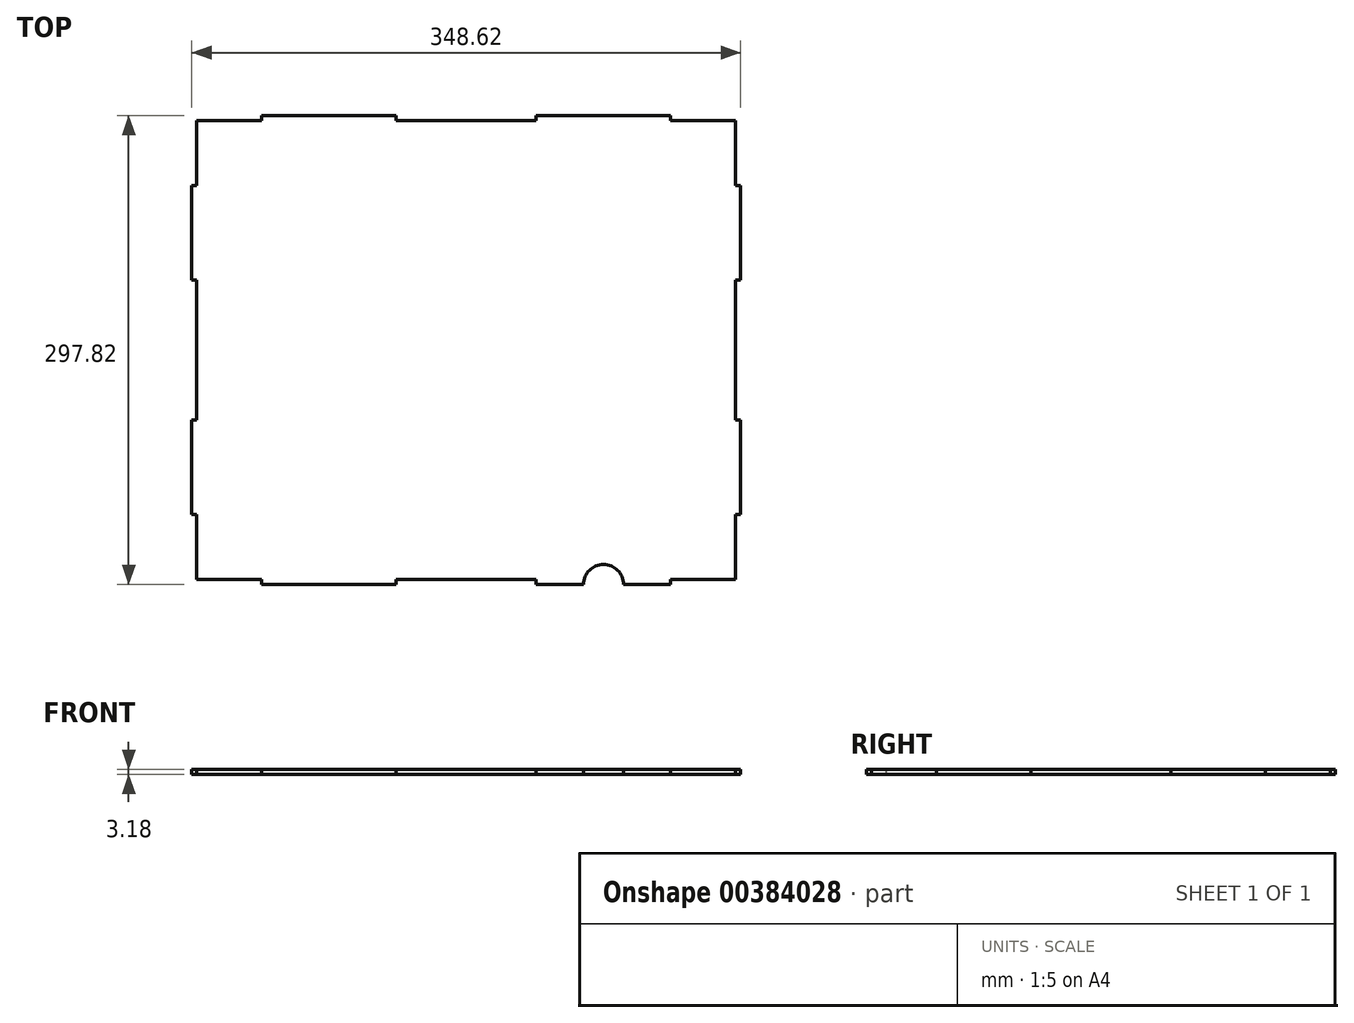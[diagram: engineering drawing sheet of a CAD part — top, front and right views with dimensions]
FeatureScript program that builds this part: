
annotation { "Feature Type Name" : "Feature", "Feature Type Description" : "" }
export const myFeature = defineFeature(function(context is Context, id is Id, definition is map)
    precondition{}
    {
        {
            var Q0;
            Q0=qCreatedBy(makeId("Top.planeOp"),FACE);
            var sketch = newSketch(context, id + "F0", { "sketchPlane" : qUnion([Q0])});
            skLineSegment(sketch, "E0.bottom", {"start": v(-174.3, 148.9) * mm, "end": v(174.3, 148.9) * mm});
            skLineSegment(sketch, "E0.top", {"start": v(-174.3, -148.9) * mm, "end": v(174.3, -148.9) * mm});
            skLineSegment(sketch, "E0.left", {"start": v(-174.3, 148.9) * mm, "end": v(-174.3, -148.9) * mm});
            skLineSegment(sketch, "E0.right", {"start": v(174.3, 148.9) * mm, "end": v(174.3, -148.9) * mm});
            skSolve(sketch);
        }
        {
            var Q0;
            Q0 = qSketchRegion(id + "F0", true);
            extrude(context, id + "F1", {"entities" : qUnion([Q0]), "depth" : 3.17 * mm});
        }
        {
            var Q0;
            Q0=makeQuery(id+"F1.opExtrude","CAP_FACE",FACE,{"disambiguationData":[OSD([sQuery(id+"F0.wireOp",EDGE,"E0.bottom"),sQuery(id+"F0.wireOp",EDGE,"E0.top"),sQuery(id+"F0.wireOp",EDGE,"E0.left"),sQuery(id+"F0.wireOp",EDGE,"E0.right")])],"isStart":false});
            var sketch = newSketch(context, id + "F2", { "sketchPlane" : qUnion([Q0])});
            skLineSegment(sketch, "E1", {"start": v(-129.86, 148.9) * mm, "end": v(-129.86, 145.73) * mm});
            skLineSegment(sketch, "E2", {"start": v(-129.86, 145.73) * mm, "end": v(-171.13, 145.73) * mm});
            skLineSegment(sketch, "E3", {"start": v(-171.13, 145.73) * mm, "end": v(-171.13, 104.46) * mm});
            skLineSegment(sketch, "E4", {"start": v(-171.13, 104.46) * mm, "end": v(-174.3, 104.46) * mm});
            skLineSegment(sketch, "E5", {"start": v(-174.3, 104.46) * mm, "end": v(-174.3, 148.9) * mm});
            skLineSegment(sketch, "E6", {"start": v(-174.3, 148.9) * mm, "end": v(-129.86, 148.9) * mm});
            skLineSegment(sketch, "E7.bottom", {"start": v(-44.45, 148.9) * mm, "end": v(0, 148.9) * mm});
            skLineSegment(sketch, "E7.top", {"start": v(-44.45, 145.73) * mm, "end": v(0, 145.73) * mm});
            skLineSegment(sketch, "E7.left", {"start": v(-44.45, 148.9) * mm, "end": v(-44.45, 145.73) * mm});
            skLineSegment(sketch, "E7.right", {"start": v(0, 148.9) * mm, "end": v(0, 145.73) * mm});
            skLineSegment(sketch, "E8.bottom", {"start": v(-174.3, 0) * mm, "end": v(-171.13, 0) * mm});
            skLineSegment(sketch, "E8.top", {"start": v(-174.3, 44.45) * mm, "end": v(-171.13, 44.45) * mm});
            skLineSegment(sketch, "E8.left", {"start": v(-174.3, 0) * mm, "end": v(-174.3, 44.45) * mm});
            skLineSegment(sketch, "E8.right", {"start": v(-171.13, 0) * mm, "end": v(-171.13, 44.45) * mm});
            skLineSegment(sketch, "E9.MirrorCS", {"start": v(44.45, 148.9) * mm, "end": v(44.45, 145.73) * mm});
            skLineSegment(sketch, "E10.MirrorCS", {"start": v(174.3, 0) * mm, "end": v(171.13, 0) * mm});
            skLineSegment(sketch, "E11.MirrorCS", {"start": v(174.3, 44.45) * mm, "end": v(171.13, 44.45) * mm});
            skLineSegment(sketch, "E12.MirrorCS", {"start": v(171.13, 104.46) * mm, "end": v(174.3, 104.46) * mm});
            skLineSegment(sketch, "E13.MirrorCS", {"start": v(129.86, 148.9) * mm, "end": v(129.86, 145.73) * mm});
            skLineSegment(sketch, "E14.MirrorCS", {"start": v(44.45, 145.73) * mm, "end": v(0, 145.73) * mm});
            skLineSegment(sketch, "E15.MirrorCS", {"start": v(174.3, 0) * mm, "end": v(174.3, 44.45) * mm});
            skLineSegment(sketch, "E16.MirrorCS", {"start": v(44.45, 148.9) * mm, "end": v(0, 148.9) * mm});
            skLineSegment(sketch, "E17.MirrorCS", {"start": v(171.13, 0) * mm, "end": v(171.13, 44.45) * mm});
            skLineSegment(sketch, "E18.MirrorCS", {"start": v(174.3, 148.9) * mm, "end": v(129.86, 148.9) * mm});
            skLineSegment(sketch, "E19.MirrorCS", {"start": v(174.3, 104.46) * mm, "end": v(174.3, 148.9) * mm});
            skLineSegment(sketch, "E20.MirrorCS", {"start": v(129.86, 145.73) * mm, "end": v(171.13, 145.73) * mm});
            skLineSegment(sketch, "E21.MirrorCS", {"start": v(171.13, 145.73) * mm, "end": v(171.13, 104.46) * mm});
            skLineSegment(sketch, "E22.MirrorCS", {"start": v(0, -148.9) * mm, "end": v(0, -145.73) * mm});
            skLineSegment(sketch, "E23.MirrorCS", {"start": v(-171.13, -104.46) * mm, "end": v(-174.3, -104.46) * mm});
            skLineSegment(sketch, "E24.MirrorCS", {"start": v(-129.86, -148.9) * mm, "end": v(-129.86, -145.73) * mm});
            skLineSegment(sketch, "E25.MirrorCS", {"start": v(44.45, -148.9) * mm, "end": v(44.45, -145.73) * mm});
            skLineSegment(sketch, "E26.MirrorCS", {"start": v(174.3, -44.45) * mm, "end": v(171.13, -44.45) * mm});
            skLineSegment(sketch, "E27.MirrorCS", {"start": v(129.86, -148.9) * mm, "end": v(129.86, -145.73) * mm});
            skLineSegment(sketch, "E28.MirrorCS", {"start": v(171.13, -104.46) * mm, "end": v(174.3, -104.46) * mm});
            skLineSegment(sketch, "E29.MirrorCS", {"start": v(-44.45, -148.9) * mm, "end": v(-44.45, -145.73) * mm});
            skLineSegment(sketch, "E30.MirrorCS", {"start": v(-174.3, -44.45) * mm, "end": v(-171.13, -44.45) * mm});
            skLineSegment(sketch, "E31.MirrorCS", {"start": v(-44.45, -148.9) * mm, "end": v(0, -148.9) * mm});
            skLineSegment(sketch, "E32.MirrorCS", {"start": v(-174.3, -148.9) * mm, "end": v(-129.86, -148.9) * mm});
            skLineSegment(sketch, "E33.MirrorCS", {"start": v(-174.3, -104.46) * mm, "end": v(-174.3, -148.9) * mm});
            skLineSegment(sketch, "E34.MirrorCS", {"start": v(-171.13, -145.73) * mm, "end": v(-171.13, -104.46) * mm});
            skLineSegment(sketch, "E35.MirrorCS", {"start": v(-129.86, -145.73) * mm, "end": v(-171.13, -145.73) * mm});
            skLineSegment(sketch, "E36.MirrorCS", {"start": v(-171.13, 0) * mm, "end": v(-171.13, -44.45) * mm});
            skLineSegment(sketch, "E37.MirrorCS", {"start": v(174.3, 0) * mm, "end": v(174.3, -44.45) * mm});
            skLineSegment(sketch, "E38.MirrorCS", {"start": v(174.3, -148.9) * mm, "end": v(129.86, -148.9) * mm});
            skLineSegment(sketch, "E39.MirrorCS", {"start": v(129.86, -145.73) * mm, "end": v(171.13, -145.73) * mm});
            skLineSegment(sketch, "E40.MirrorCS", {"start": v(44.45, -145.73) * mm, "end": v(0, -145.73) * mm});
            skLineSegment(sketch, "E41.MirrorCS", {"start": v(44.45, -148.9) * mm, "end": v(0, -148.9) * mm});
            skLineSegment(sketch, "E42.MirrorCS", {"start": v(171.13, 0) * mm, "end": v(171.13, -44.45) * mm});
            skLineSegment(sketch, "E43.MirrorCS", {"start": v(-44.45, -145.73) * mm, "end": v(0, -145.73) * mm});
            skLineSegment(sketch, "E44.MirrorCS", {"start": v(174.3, -104.46) * mm, "end": v(174.3, -148.9) * mm});
            skLineSegment(sketch, "E45.MirrorCS", {"start": v(171.13, -145.73) * mm, "end": v(171.13, -104.46) * mm});
            skLineSegment(sketch, "E46.MirrorCS", {"start": v(-174.3, 0) * mm, "end": v(-174.3, -44.45) * mm});
            skSolve(sketch);
        }
        {
            var Q0;
            Q0 = qSketchRegion(id + "F2", true);
            extrude(context, id + "F3", {"entities" : qUnion([Q0]), "operationType" : NewBodyOperationType.REMOVE, "endBound" : BoundingType.THROUGH_ALL, "oppositeDirection" : true, "depth" : 25.4 * mm});
        }
        {
            var Q0;
            Q0=makeQuery(id+"F1.opExtrude","CAP_FACE",FACE,{"disambiguationData":[OSD([sQuery(id+"F0.wireOp",EDGE,"E0.bottom"),sQuery(id+"F0.wireOp",EDGE,"E0.top"),sQuery(id+"F0.wireOp",EDGE,"E0.left"),sQuery(id+"F0.wireOp",EDGE,"E0.right")])],"isStart":false});
            var sketch = newSketch(context, id + "F4", { "sketchPlane" : qUnion([Q0])});
            skArc(sketch, "E47", {"start": v(99.85, -148.9) * mm, "mid": v(87.15, -136.2) * mm, "end": v(74.45, -148.9) * mm});
            skLineSegment(sketch, "E48", {"start": v(74.45, -148.9) * mm, "end": v(99.85, -148.9) * mm});
            skSolve(sketch);
        }
        {
            var Q0;
            Q0 = qSketchRegion(id + "F4", true);
            extrude(context, id + "F5", {"entities" : qUnion([Q0]), "operationType" : NewBodyOperationType.REMOVE, "endBound" : BoundingType.THROUGH_ALL, "oppositeDirection" : true, "depth" : 25.4 * mm});
        }
    });
